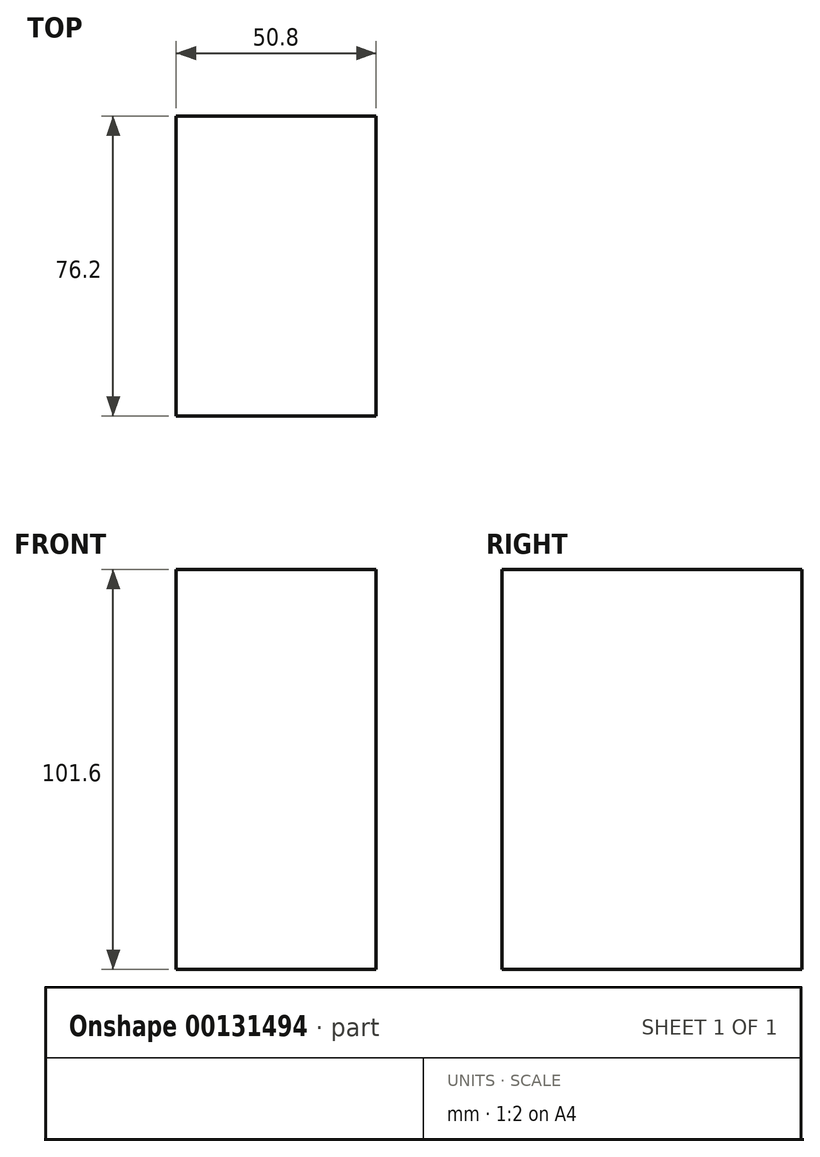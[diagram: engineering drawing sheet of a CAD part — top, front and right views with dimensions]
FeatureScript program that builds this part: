
annotation { "Feature Type Name" : "Feature", "Feature Type Description" : "" }
export const myFeature = defineFeature(function(context is Context, id is Id, definition is map)
    precondition{}
    {
        {
            var Q0;
            Q0=qCreatedBy(makeId("Front.planeOp"),FACE);
            var sketch = newSketch(context, id + "F0", { "sketchPlane" : qUnion([Q0])});
            skLineSegment(sketch, "E0.bottom", {"start": v(-25.4, -50.8) * mm, "end": v(25.4, -50.8) * mm});
            skLineSegment(sketch, "E0.top", {"start": v(-25.4, 50.8) * mm, "end": v(25.4, 50.8) * mm});
            skLineSegment(sketch, "E0.left", {"start": v(-25.4, -50.8) * mm, "end": v(-25.4, 50.8) * mm});
            skLineSegment(sketch, "E0.right", {"start": v(25.4, -50.8) * mm, "end": v(25.4, 50.8) * mm});
            skPoint(sketch, "E0.middle", {"position": v(0, 0) * mm});
            skSolve(sketch);
        }
        {
            var Q0;
            Q0 = qSketchRegion(id + "F0", true);
            extrude(context, id + "F1", {"entities" : qUnion([Q0]), "depth" : 76.2 * mm});
        }
    });
